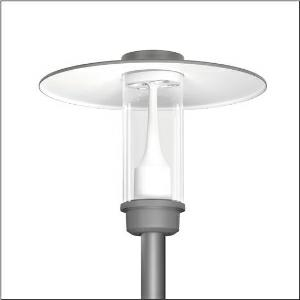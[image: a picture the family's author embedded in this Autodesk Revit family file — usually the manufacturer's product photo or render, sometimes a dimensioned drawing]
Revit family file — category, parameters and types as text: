
# Revit family: litepole_2_iq___st1_2a_5xa5425mf14h_5009
name_source: partatom
category: Lighting Fixtures
units: mm (PartAtom-declared; Revit-internal decimal feet)

## family parameters
Cut with Voids When Loaded = No
Host = Face
Light Source = No
Part Type = Normal
Room Calculation Point = No
Round Connector Dimension = Use Diameter
Shared = No

## types (1)
- --- (1 x LED, 1550 lm, 11.8 W, 2700K)
    Apparent Load = 12 VA
    CIE Flux Codes = 22 60 92 98 100
    Color Rendering = 70
    Color Temperature = 2700K
    Default Elevation = 1800 mm
    Description = Litepole 2 iQ, mast luminaire, Module 540 iQ-SR, primary light control with 3 zone facetted reflector, of plastic, silver coated, highly specular, structured, primary optical cover: cover, of PMMA, transparent, light distribution: ST1.2a, light emission: direct distribution, primary light characteristic: asymmetric, installation type: post-top, LED, High Power LED, rated luminous flux: 1.550lm, luminous efficacy: 131lm/W, light colour: 727, colour temperature: 2700K, control gear: iQ Street-Remote, control: pre-setting: logarithmic dimming characteristic, Street-Remote, Auto-Match, Temp-Guard, Lumen-Switch, Night-Set, Smart-Wire, Light-Fading, Desk-Remote (wireless, voltage-free reading and setting of iQ features in the workshop via application-optimized NFC function/RFID function), optimised constant luminous flux control (CLO 2.0), with terminal, 6-pole, max. 2.5mm², mains connection: 230..240V, AC, 50/60Hz, start of lifetime: 12W, end of service life: 12W, reduction: 6W, luminaire housing, upper part, of aluminium, coated, Siteco® metallic grey (DB 702S), diameter: 750mm, height: 590mm, spigot size: d x l = 76 x 70mm (post-top) | with reducer (optional accessory) 60 x 70mm, mounting height: 3..5m, post-top mast mounting element, of diecast aluminium, coated, Siteco® metallic grey (DB 702S), Module 540 iQ-SR, traffic white (RAL 9016), equipment: standard, protection rating (complete): IP65, insulation class (complete): insulation class II (safety insulation), certification: CE, ENEC, VDE, packaging unit: 1 piece

Light Distribution: ST1.2a
    Height = 590 mm
    Lamp = 1 x LED
    Lamp Light Flux = 1550 lm
    Lamp Power = 11.8 W
    Lamp count = 1
    Length = 750 mm
    Luminous efficacy = 131 lm/W
    Manufacturer = Siteco
    ModVariant = No
    Model = 5XA5425MF14H
    Number of Poles = 1
    OnlyDefault = Yes
    Power Factor = 1
    Product Name = Litepole 2 iQ | ST1.2a
    Product group = mast luminaire | pylon top
    ProductGroupID = 6100
    Protection Class = Protection class II
    Protection Degree = IP 65
    RLX_Detail_Level = 1
    RLX_Emergency_Light_Flux = 0 lm
    RLX_Emergency_Type = 0
    RLX_Emergency_Type_DB = No
    RlxData = <blob elided: 63945 chars, md5=6245bb5f>
    Socket = socket
    Standby Power = 0 W
    System Light Flux = 1550 lm
    System Power = 12 W
    Type Comments = factory setting: luminous flux: 100 % | dim-lin: 254 | 472 mA
    Type Image = l_1006518.jpg
    URL = http://relux.com
    VarID = @adj_173913
    Voltage = 0 V
    Weight = 0.00 kg
    Width = 0 mm  [stored 0 ft]

note: [stored X ft] marks values corroborated as IEEE doubles in the binary element streams (Revit-internal decimal feet)

## geometry (parser evidence)
native form markers: Blend x4, Sweep x10
no freeform markers — native parametric forms only
